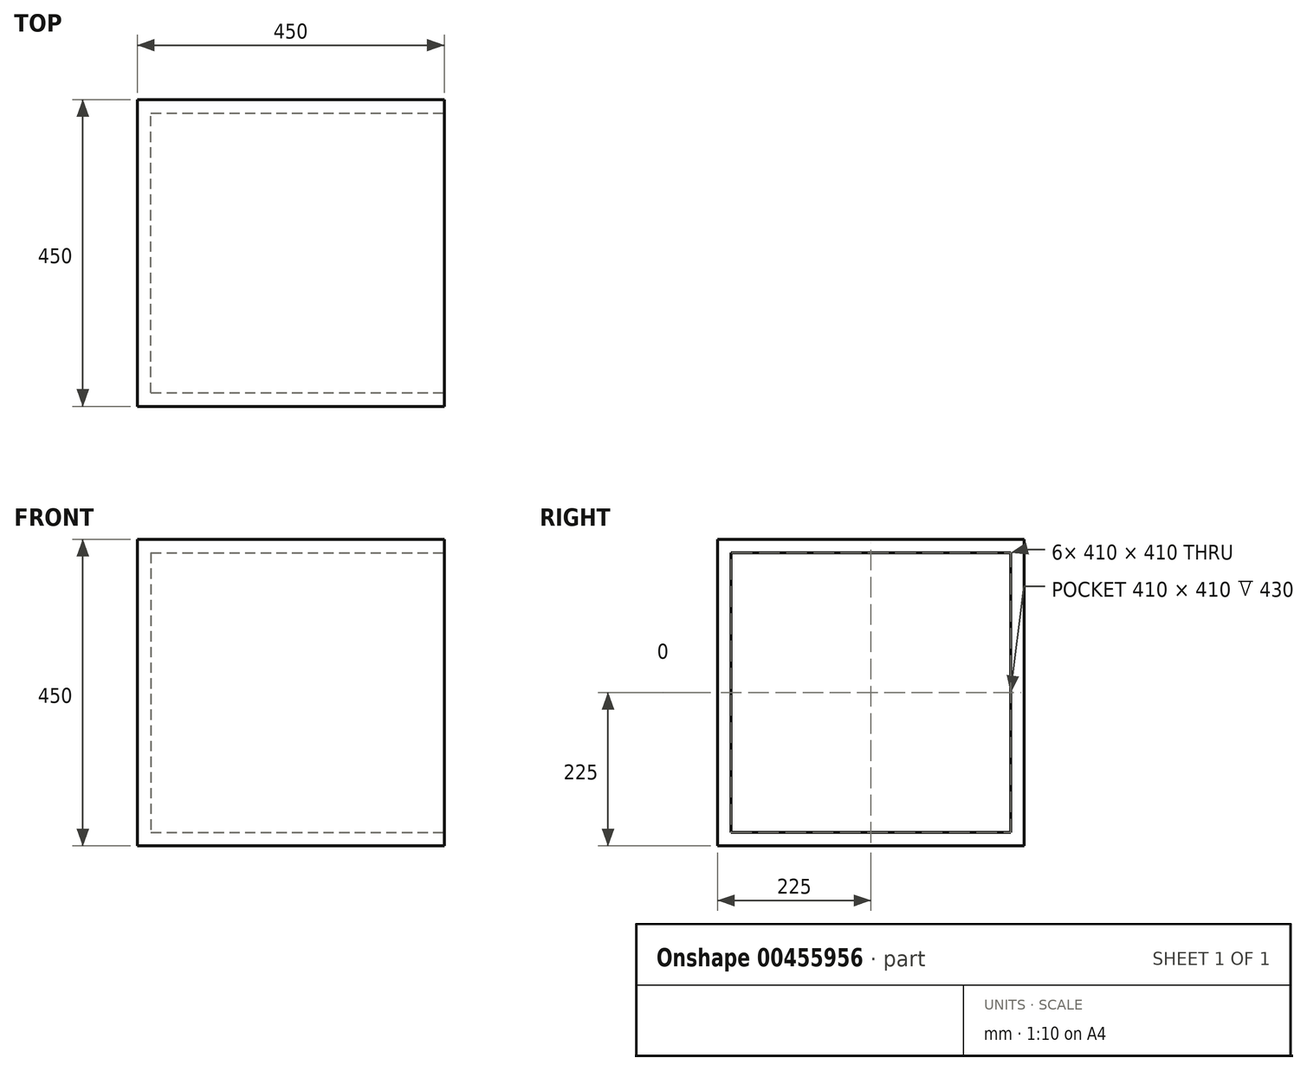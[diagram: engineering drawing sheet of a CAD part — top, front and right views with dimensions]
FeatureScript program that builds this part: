
annotation { "Feature Type Name" : "Feature", "Feature Type Description" : "" }
export const myFeature = defineFeature(function(context is Context, id is Id, definition is map)
    precondition{}
    {
        {
            var Q0;
            Q0=qCreatedBy(makeId("Front.planeOp"),FACE);
            var sketch = newSketch(context, id + "F0", { "sketchPlane" : qUnion([Q0])});
            skLineSegment(sketch, "E0.bottom", {"start": v(-13273.49, 450) * mm, "end": v(-12823.49, 450) * mm});
            skLineSegment(sketch, "E0.top", {"start": v(-13273.49, 0) * mm, "end": v(-12823.49, 0) * mm});
            skLineSegment(sketch, "E0.left", {"start": v(-13273.49, 450) * mm, "end": v(-13273.49, 0) * mm});
            skLineSegment(sketch, "E0.right", {"start": v(-12823.49, 450) * mm, "end": v(-12823.49, 0) * mm});
            skSolve(sketch);
        }
        {
            var Q0;
            Q0=makeQuery(id+"F0.imprint","IMPRINT",FACE,{"disambiguationData":[TD([[makeQuery(id+"F0.imprint","IMPRINT",EDGE,{"derivedFrom":sQuery(id+"F0.wireOp",EDGE,"E0.bottom")}),-1.0]])]});
            var Q1;
            Q1=sQuery(id+"F0.wireOp",EDGE,"E0.right");
            var Q2;
            Q2=sQuery(id+"F0.wireOp",EDGE,"E0.bottom");
            var Q3;
            Q3=sQuery(id+"F0.wireOp",EDGE,"E0.left");
            var Q4;
            Q4=sQuery(id+"F0.wireOp",EDGE,"E0.top");
            extrude(context, id + "F1", {"entities" : qUnion([Q0]), "surfaceEntities" : qUnion([Q1, Q2, Q3, Q4]), "depth" : 450 * mm});
        }
        {
            var Q0;
            Q0=makeQuery(id+"F1.opExtrude","SWEPT_FACE",FACE,{"disambiguationData":[OSD([sQuery(id+"F0.wireOp",EDGE,"E0.right")])]});
            shell(context, id + "F2", {"entities" : qUnion([Q0]), "thickness" : 20 * mm});
        }
    });
